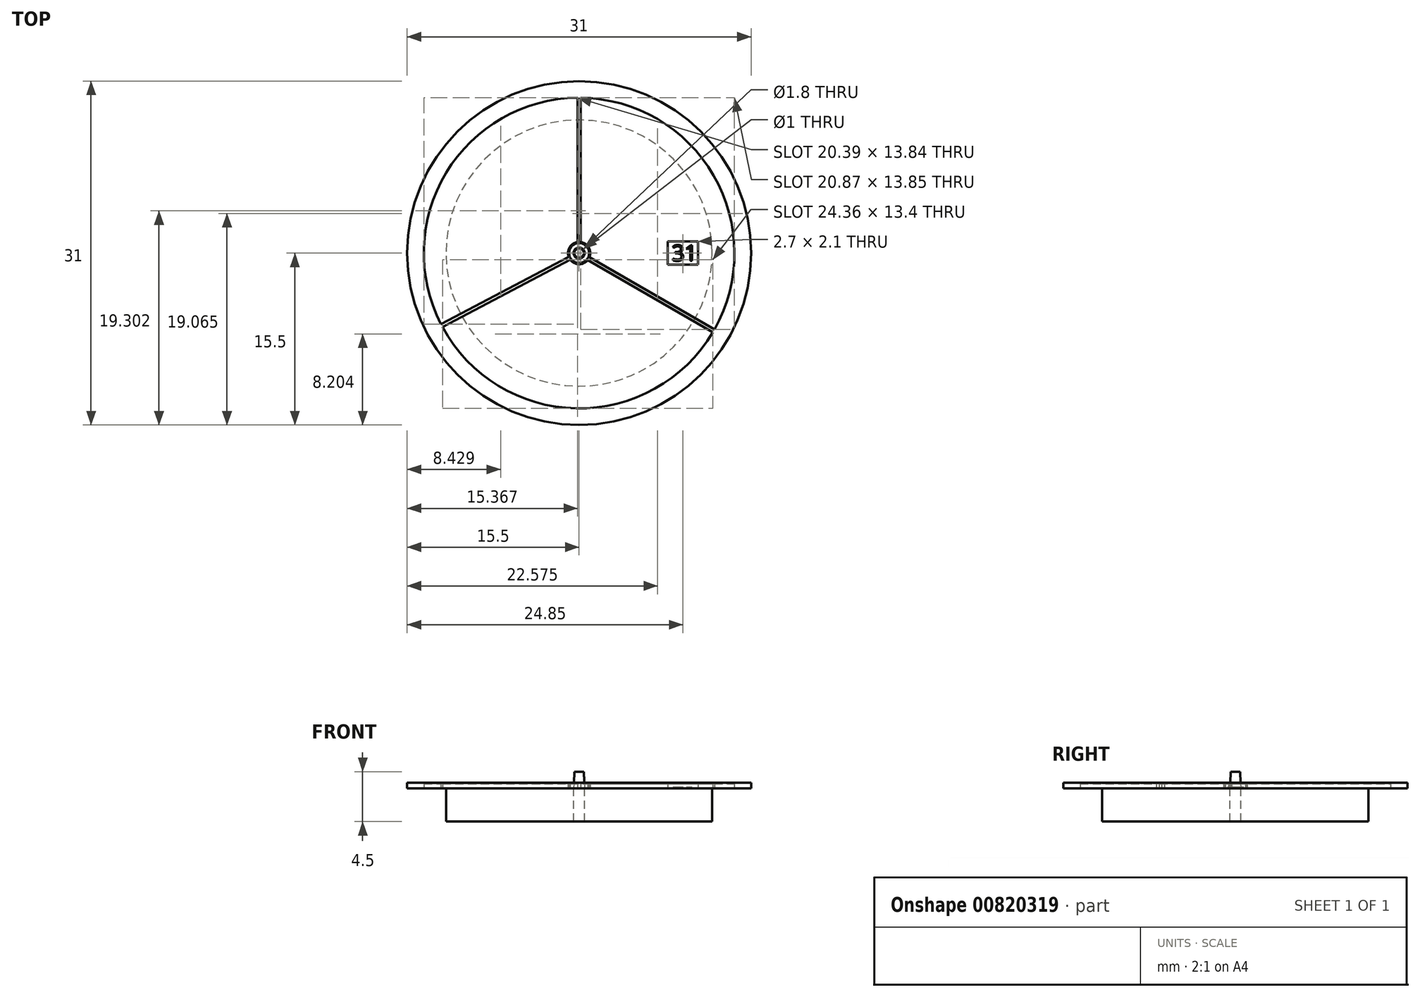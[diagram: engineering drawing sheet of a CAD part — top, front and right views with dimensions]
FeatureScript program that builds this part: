
annotation { "Feature Type Name" : "Feature", "Feature Type Description" : "" }
export const myFeature = defineFeature(function(context is Context, id is Id, definition is map)
    precondition{}
    {
        {
            var Q0;
            Q0=qCreatedBy(makeId("Top.planeOp"),FACE);
            var sketch = newSketch(context, id + "F0", { "sketchPlane" : qUnion([Q0])});
            skCircle(sketch, "E0", {"center": v(0, 0) * mm, "radius": 15.5 * mm});
            skArc(sketch, "E1", {"start": v(12.2, -6.87) * mm, "mid": v(12.12, 7) * mm, "end": v(0.15, 14) * mm});
            skLineSegment(sketch, "E2.0", {"start": v(0.78, -0.62) * mm, "end": v(12.05, -7.13) * mm});
            skLineSegment(sketch, "E3.0", {"start": v(0.93, -0.36) * mm, "end": v(12.2, -6.87) * mm});
            skLineSegment(sketch, "E4.0", {"start": v(-0.15, 14) * mm, "end": v(-0.15, 0.99) * mm});
            skLineSegment(sketch, "E5.0", {"start": v(-0.8, -0.6) * mm, "end": v(-12.31, -6.66) * mm});
            skLineSegment(sketch, "E6.0", {"start": v(0.15, 14) * mm, "end": v(0.15, 0.99) * mm});
            skArc(sketch, "E7", {"start": v(0.93, -0.36) * mm, "mid": v(0.87, 0.5) * mm, "end": v(0.15, 0.99) * mm});
            skPoint(sketch, "E8.orphan", {"position": v(0, 14) * mm});
            skLineSegment(sketch, "E9.trimOffspring", {"start": v(-0.94, -0.33) * mm, "end": v(-12.45, -6.4) * mm});
            skArc(sketch, "E10.trimOffspring", {"start": v(-0.8, -0.6) * mm, "mid": v(-0.02, -1) * mm, "end": v(0.78, -0.62) * mm});
            skArc(sketch, "E11.trimOffspring", {"start": v(-0.15, 0.99) * mm, "mid": v(-0.86, 0.52) * mm, "end": v(-0.94, -0.33) * mm});
            skArc(sketch, "E12.trimOffspring", {"start": v(-12.31, -6.66) * mm, "mid": v(-0.27, -14) * mm, "end": v(12.05, -7.13) * mm});
            skArc(sketch, "E13.trimOffspring", {"start": v(-0.15, 14) * mm, "mid": v(-11.99, 7.23) * mm, "end": v(-12.45, -6.4) * mm});
            skCircle(sketch, "E14", {"center": v(0, 0) * mm, "radius": 0.9 * mm});
            skCircle(sketch, "E15", {"center": v(0, 0) * mm, "radius": 12 * mm});
            skCircle(sketch, "E16", {"center": v(0, 0) * mm, "radius": 0.5 * mm});
            skLineSegment(sketch, "E17.bottom", {"start": v(8, 1.05) * mm, "end": v(10.7, 1.05) * mm});
            skLineSegment(sketch, "E17.top", {"start": v(8, -1.05) * mm, "end": v(10.7, -1.05) * mm});
            skLineSegment(sketch, "E17.left", {"start": v(8, 1.05) * mm, "end": v(8, -1.05) * mm});
            skLineSegment(sketch, "E17.right", {"start": v(10.7, 1.05) * mm, "end": v(10.7, -1.05) * mm});
            skText(sketch, "E18", { "text": "31", "fontName": "OpenSans-Regular.ttf"});
            const initialGuessF0  = {"E18": [0.00836, -0.0007, 1, 0, 0.00143]};
            skSetInitialGuess(sketch, initialGuessF0);
            skSolve(sketch);
        }
        {
            var Q0;
            {var subQ0=sQuery(id+"F0.wireOp",EDGE,"E7");Q0=makeQuery(id+"F0.imprint","IMPRINT",FACE,{"disambiguationData":[TD([[makeQuery(id+"F0.imprint","IMPRINT",EDGE,{"derivedFrom":subQ0}),-1.0]])]});}
            var Q1;
            {var subQ0=sQuery(id+"F0.wireOp",EDGE,"E11.trimOffspring");Q1=makeQuery(id+"F0.imprint","IMPRINT",FACE,{"disambiguationData":[TD([[makeQuery(id+"F0.imprint","IMPRINT",EDGE,{"derivedFrom":subQ0}),-1.0]])]});}
            var Q2;
            {var subQ0=sQuery(id+"F0.wireOp",EDGE,"E10.trimOffspring");Q2=makeQuery(id+"F0.imprint","IMPRINT",FACE,{"disambiguationData":[TD([[makeQuery(id+"F0.imprint","IMPRINT",EDGE,{"derivedFrom":subQ0}),-1.0]])]});}
            var Q3;
            Q3=makeQuery(id+"F0.imprint","IMPRINT",FACE,{"disambiguationData":[TD([[makeQuery(id+"F0.imprint","IMPRINT",EDGE,{"derivedFrom":sQuery(id+"F0.wireOp",EDGE,"E14")}),1.0]])]});
            var Q4;
            {var subQ1=sQuery(id+"F0.wireOp",EDGE,"E7");Q4=makeQuery(id+"F0.imprint","IMPRINT",FACE,{"disambiguationData":[TD([[makeQuery(id+"F0.imprint","IMPRINT",EDGE,{"derivedFrom":subQ1}),1.0]])]});}
            var Q5;
            Q5=makeQuery(id+"F0.imprint","IMPRINT",FACE,{"disambiguationData":[TD([[makeQuery(id+"F0.imprint","IMPRINT",EDGE,{"derivedFrom":sQuery(id+"F0.wireOp",EDGE,"E17.bottom")}),-1.0]])]});
            var Q6;
            Q6=makeQuery(id+"F0.imprint","IMPRINT",FACE,{"disambiguationData":[TD([[makeQuery(id+"F0.imprint","IMPRINT",EDGE,{"derivedFrom":sQuery(id+"F0.wireOp",EDGE,"E18.sketch_text.stroke-28")}),-1.0]])]});
            var Q7;
            Q7=makeQuery(id+"F0.imprint","IMPRINT",FACE,{"disambiguationData":[TD([[makeQuery(id+"F0.imprint","IMPRINT",EDGE,{"derivedFrom":sQuery(id+"F0.wireOp",EDGE,"E18.sketch_text.stroke-0")}),-1.0]])]});
            extrude(context, id + "F1", {"entities" : qUnion([Q0, Q1, Q2, Q3, Q4, Q5, Q6, Q7]), "oppositeDirection" : true, "depth" : 3 * mm, "offsetDistance" : 25 * mm});
        }
        {
            var Q0;
            Q0 = qSketchRegion(id + "F0", true);
            var Q1;
            {var subQ1=sQuery(id+"F0.wireOp",EDGE,"E7");Q1=makeQuery(id+"F0.imprint","IMPRINT",FACE,{"disambiguationData":[TD([[makeQuery(id+"F0.imprint","IMPRINT",EDGE,{"derivedFrom":subQ1}),1.0]])]});}
            extrude(context, id + "F2", {"entities" : qUnion([Q0, Q1]), "depth" : 0.5 * mm, "offsetDistance" : 25 * mm});
        }
        {
            var Q0;
            {var subQ0=sQuery(id+"F0.wireOp",EDGE,"E1");Q0=makeQuery(id+"F0.imprint","IMPRINT",FACE,{"disambiguationData":[TD([[makeQuery(id+"F0.imprint","IMPRINT",EDGE,{"derivedFrom":subQ0}),1.0]])]});}
            var Q1;
            {var subQ0=sQuery(id+"F0.wireOp",EDGE,"E7");Q1=makeQuery(id+"F0.imprint","IMPRINT",FACE,{"disambiguationData":[TD([[makeQuery(id+"F0.imprint","IMPRINT",EDGE,{"derivedFrom":subQ0}),-1.0]])]});}
            var Q2;
            {var subQ0=sQuery(id+"F0.wireOp",EDGE,"E13.trimOffspring");Q2=makeQuery(id+"F0.imprint","IMPRINT",FACE,{"disambiguationData":[TD([[makeQuery(id+"F0.imprint","IMPRINT",EDGE,{"derivedFrom":subQ0}),1.0]])]});}
            var Q3;
            {var subQ0=sQuery(id+"F0.wireOp",EDGE,"E11.trimOffspring");Q3=makeQuery(id+"F0.imprint","IMPRINT",FACE,{"disambiguationData":[TD([[makeQuery(id+"F0.imprint","IMPRINT",EDGE,{"derivedFrom":subQ0}),-1.0]])]});}
            var Q4;
            {var subQ0=sQuery(id+"F0.wireOp",EDGE,"E10.trimOffspring");Q4=makeQuery(id+"F0.imprint","IMPRINT",FACE,{"disambiguationData":[TD([[makeQuery(id+"F0.imprint","IMPRINT",EDGE,{"derivedFrom":subQ0}),-1.0]])]});}
            var Q5;
            {var subQ0=sQuery(id+"F0.wireOp",EDGE,"E12.trimOffspring");Q5=makeQuery(id+"F0.imprint","IMPRINT",FACE,{"disambiguationData":[TD([[makeQuery(id+"F0.imprint","IMPRINT",EDGE,{"derivedFrom":subQ0}),1.0]])]});}
            extrude(context, id + "F3", {"entities" : qUnion([Q0, Q1, Q2, Q3, Q4, Q5]), "depth" : 0.4 * mm, "offsetDistance" : 25 * mm});
        }
        {
            var Q0;
            Q0=makeQuery(id+"F0.imprint","IMPRINT",FACE,{"disambiguationData":[TD([[makeQuery(id+"F0.imprint","IMPRINT",EDGE,{"derivedFrom":sQuery(id+"F0.wireOp",EDGE,"E16")}),1.0]])]});
            extrude(context, id + "F4", {"entities" : qUnion([Q0]), "depth" : 1.5 * mm, "offsetDistance" : 25 * mm, "hasDraft" : true, "draftAngle" : 3 * degree, "draftPullDirection" : true});
        }
        {
            var Q0;
            Q0=makeQuery(id+"F0.imprint","IMPRINT",FACE,{"disambiguationData":[TD([[makeQuery(id+"F0.imprint","IMPRINT",EDGE,{"derivedFrom":sQuery(id+"F0.wireOp",EDGE,"E18.sketch_text.stroke-0")}),-1.0]])]});
            var Q1;
            Q1=makeQuery(id+"F0.imprint","IMPRINT",FACE,{"disambiguationData":[TD([[makeQuery(id+"F0.imprint","IMPRINT",EDGE,{"derivedFrom":sQuery(id+"F0.wireOp",EDGE,"E18.sketch_text.stroke-28")}),-1.0]])]});
            extrude(context, id + "F5", {"entities" : qUnion([Q0, Q1]), "operationType" : NewBodyOperationType.ADD, "depth" : 0.1 * mm, "offsetDistance" : 25 * mm});
        }
    });
